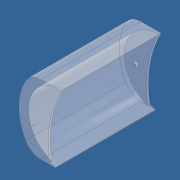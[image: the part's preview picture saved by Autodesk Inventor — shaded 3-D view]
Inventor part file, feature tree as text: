
AUTODESK INVENTOR PART (.ipt)
format: ipt  version: 2021 (Build 250183000, 183)  size: 168,448 bytes
history: native  units: mm
features: extrude x3, sketch x3, mirror x1
ambient origin geometry x8: Origin, YZ Plane, XZ Plane, XY Plane, X Axis, Y Axis, Z Axis, Center Point
bodies: Solid1 (feature_tree)
feature tree (7):
  extrude  "Extrusion1"  Depth=10.0mm TaperAngle=0.0deg
  extrude  "Extrusion2"  Depth=160.0mm
  extrude  "Extrusion9"  Depth=9.7mm
  mirror  "Mirror4"
  sketch  "Sketch1"  dims[d6=442.6mm d7=0.0mm d12=10.0mm d13=0.0mm]
  sketch  "Sketch2"  dims[d53=160.0mm d55=68.151999mm]
  sketch  "Sketch10"  dims[d56=80.0mm d60=92.094435mm d65=1.0mm d66=484.72575mm d71=246.817107mm d72=80.0mm d73=160.0mm d74=68.151999mm d75=80.0mm d76=92.094435mm d77=1.0mm d78=484.72575mm d79=246.817107mm d80=80.0mm d81=18.0mm d82=130.0mm d83=99.796214mm d84=9.7mm d85=0.0mm d26=0.5mm d27=0.872665mm d28=0.5mm d29=0.872665mm d30=0.5mm d31=0.872665mm d32=0.5mm d33=0.872665mm]
